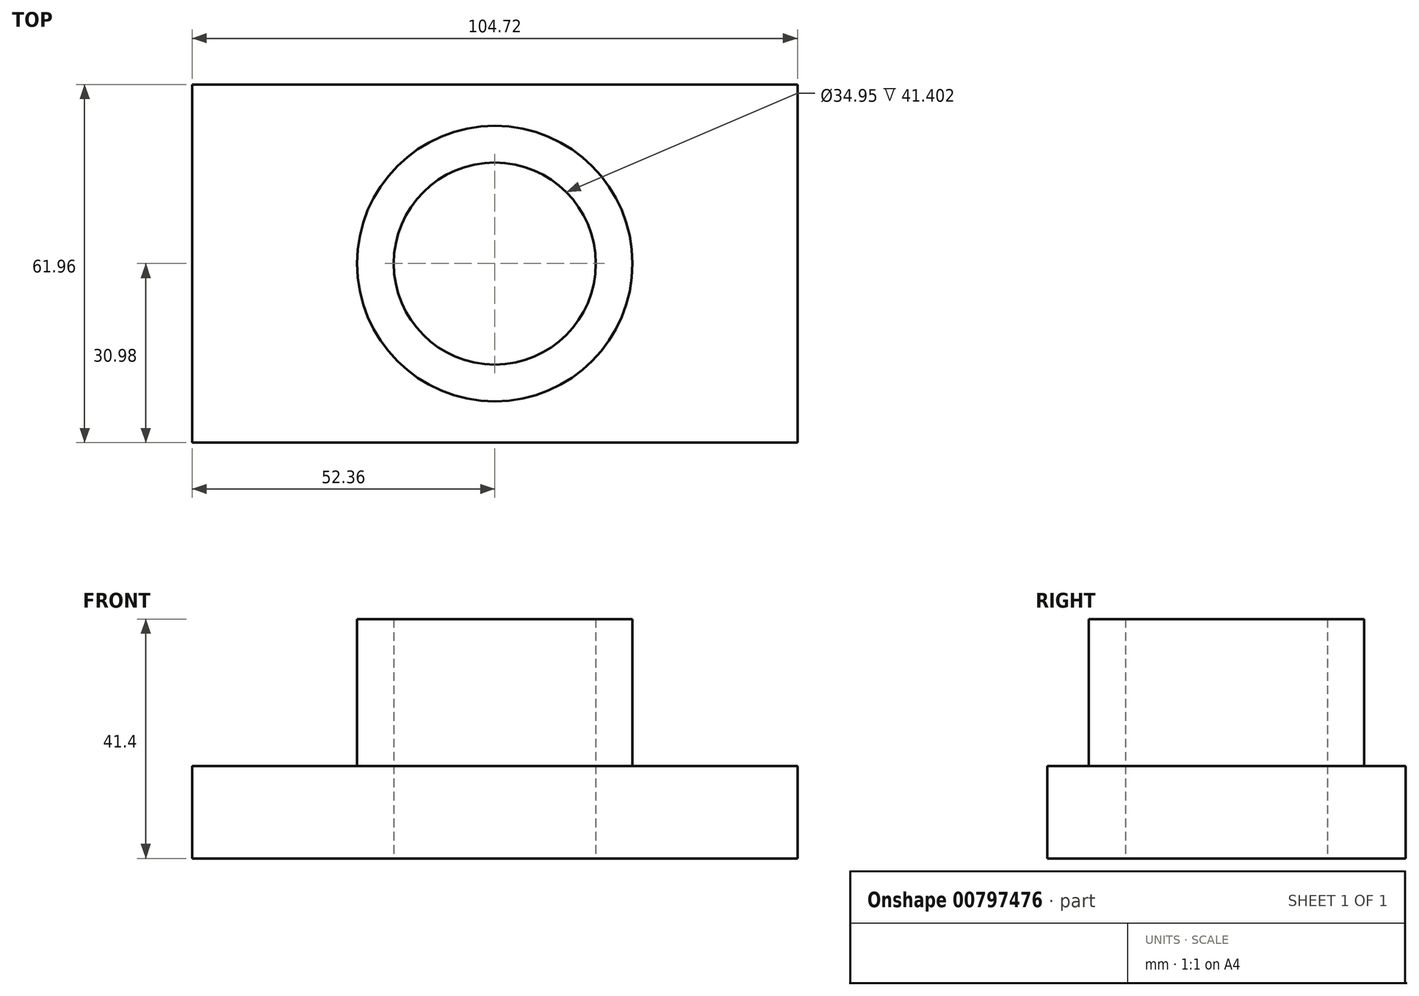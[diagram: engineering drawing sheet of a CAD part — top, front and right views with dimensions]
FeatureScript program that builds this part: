
annotation { "Feature Type Name" : "Feature", "Feature Type Description" : "" }
export const myFeature = defineFeature(function(context is Context, id is Id, definition is map)
    precondition{}
    {
        {
            var Q0;
            Q0=qCreatedBy(makeId("Top.planeOp"),FACE);
            var sketch = newSketch(context, id + "F0", { "sketchPlane" : qUnion([Q0])});
            skLineSegment(sketch, "E0.bottom", {"start": v(-52.36, 30.98) * mm, "end": v(52.36, 30.98) * mm});
            skLineSegment(sketch, "E0.top", {"start": v(-52.36, -30.98) * mm, "end": v(52.36, -30.98) * mm});
            skLineSegment(sketch, "E0.left", {"start": v(-52.36, 30.98) * mm, "end": v(-52.36, -30.98) * mm});
            skLineSegment(sketch, "E0.right", {"start": v(52.36, 30.98) * mm, "end": v(52.36, -30.98) * mm});
            skPoint(sketch, "E0.middle", {"position": v(0, 0) * mm});
            skSolve(sketch);
        }
        {
            var Q0;
            Q0 = qSketchRegion(id + "F0", true);
            extrude(context, id + "F1", {"entities" : qUnion([Q0]), "depth" : 16 * mm, "offsetDistance" : 25.4 * mm});
        }
        {
            var Q0;
            Q0=makeQuery(id+"F1.opExtrude","CAP_FACE",FACE,{"disambiguationData":[OSD([sQuery(id+"F0.wireOp",EDGE,"E0.bottom"),sQuery(id+"F0.wireOp",EDGE,"E0.top"),sQuery(id+"F0.wireOp",EDGE,"E0.left"),sQuery(id+"F0.wireOp",EDGE,"E0.right")])],"isStart":false});
            var sketch = newSketch(context, id + "F2", { "sketchPlane" : qUnion([Q0])});
            skCircle(sketch, "E1", {"center": v(0, 0) * mm, "radius": 17.47 * mm});
            skCircle(sketch, "E2.0", {"center": v(0, 0) * mm, "radius": 23.82 * mm});
            skSolve(sketch);
        }
        {
            var Q0;
            Q0=makeQuery(id+"F2.imprint","IMPRINT",FACE,{"disambiguationData":[TD([[makeQuery(id+"F2.imprint","IMPRINT",EDGE,{"derivedFrom":sQuery(id+"F2.wireOp",EDGE,"E1")}),-1.0]])]});
            extrude(context, id + "F3", {"entities" : qUnion([Q0]), "operationType" : NewBodyOperationType.ADD, "depth" : 25.4 * mm, "offsetDistance" : 25.4 * mm});
        }
        {
            var Q0;
            Q0=makeQuery(id+"F3.boolean.opBoolean","SPLIT",FACE,{"disambiguationData":[TD([makeQuery(id+"F3.opExtrude","SWEPT_FACE",FACE,{"disambiguationData":[OSD([sQuery(id+"F2.wireOp",EDGE,"E1")])]})])],"derivedFrom":makeQuery(id+"F1.opExtrude","CAP_FACE",FACE,{"disambiguationData":[OSD([sQuery(id+"F0.wireOp",EDGE,"E0.bottom"),sQuery(id+"F0.wireOp",EDGE,"E0.top"),sQuery(id+"F0.wireOp",EDGE,"E0.left"),sQuery(id+"F0.wireOp",EDGE,"E0.right")])],"isStart":false})});
            extrude(context, id + "F4", {"entities" : qUnion([Q0]), "operationType" : NewBodyOperationType.REMOVE, "oppositeDirection" : true, "depth" : 25.4 * mm, "offsetDistance" : 25.4 * mm});
        }
    });
